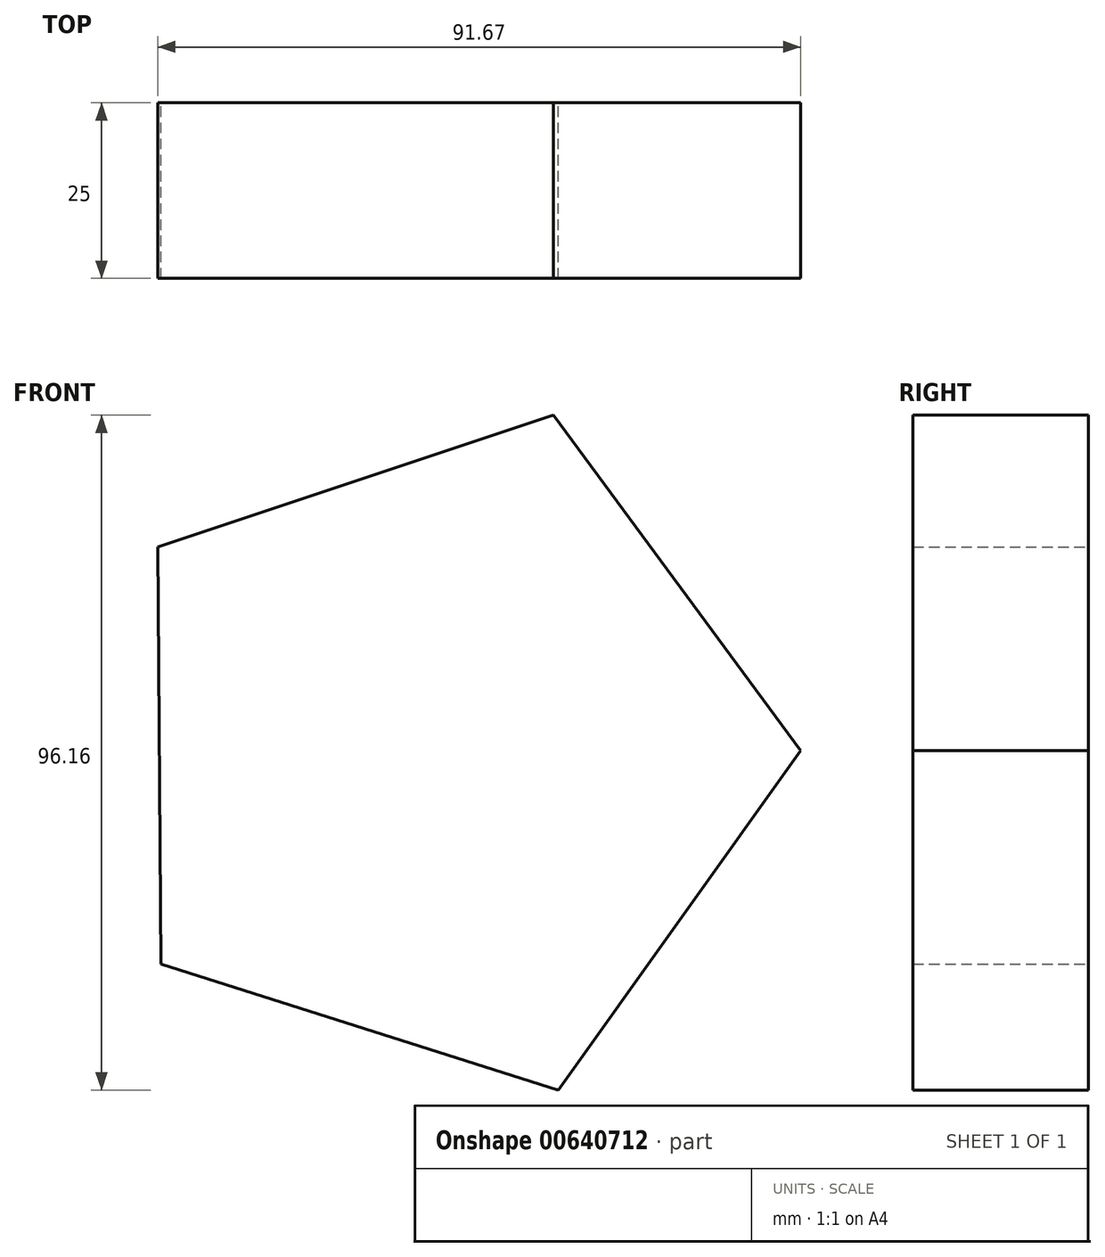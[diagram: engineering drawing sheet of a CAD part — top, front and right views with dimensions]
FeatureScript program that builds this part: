
annotation { "Feature Type Name" : "Feature", "Feature Type Description" : "" }
export const myFeature = defineFeature(function(context is Context, id is Id, definition is map)
    precondition{}
    {
        {
            var Q0;
            Q0=qCreatedBy(makeId("Front.planeOp"),FACE);
            var sketch = newSketch(context, id + "F0", { "sketchPlane" : qUnion([Q0])});
            skCircle(sketch, "E0.cCircle", {"center": v(0, 0) * mm, "radius": 40.9 * mm, "construction": true});
            skLineSegment(sketch, "E0.0", {"start": v(15.26, 48.2) * mm, "end": v(50.55, 0.38) * mm});
            skLineSegment(sketch, "E0.1", {"start": v(50.55, 0.38) * mm, "end": v(15.98, -47.96) * mm});
            skLineSegment(sketch, "E0.2", {"start": v(15.98, -47.96) * mm, "end": v(-40.68, -30.02) * mm});
            skLineSegment(sketch, "E0.3", {"start": v(-40.68, -30.02) * mm, "end": v(-41.12, 29.4) * mm});
            skLineSegment(sketch, "E0.4", {"start": v(-41.12, 29.4) * mm, "end": v(15.26, 48.2) * mm});
            skPoint(sketch, "E0.0.midPoint", {"position": v(32.9, 24.29) * mm});
            skSolve(sketch);
        }
        {
            var Q0;
            Q0 = qSketchRegion(id + "F0", true);
            extrude(context, id + "F1", {"entities" : qUnion([Q0]), "depth" : 25 * mm, "offsetDistance" : 25 * mm});
        }
    });
